# Revit family: Gohome_ClubOttoman_R19
name_source: partatom
category: Furniture
units: mm (PartAtom-declared; Revit-internal decimal feet)

## family parameters
Always vertical = Yes
Cut with Voids When Loaded = No
OmniClass Number = 23.40.20.00
OmniClass Title = General Furniture and Specialties
Room Calculation Point = No
Shared = No
Work Plane-Based = No

## types (4) — shared parameters
Depth = 700 mm  [stored 2.29659 ft]
Manufacturer = gohome
Seat Height = 450 mm  [stored 1.47638 ft]
Timber Leg Material = <By Category>
URL = www.gohome.com.au
Upholstery Material = <By Category>
Width = 1800 mm  [stored 5.90551 ft]

## per-type parameters (varying)
| type | Height | ShowCenterBottomLeg | ShowCenterTopLeg | ShowEndLeg | With Bolster | With Tabletop Center | With Tabletop End |
| Club Ottoman w/4 Legs | 450 mm  [stored 1.47638 ft] | Yes | Yes | Yes | No | No | No |
| Club Ottoman w/Bolster | 605 mm  [stored 1.98491 ft] | No | No | Yes | Yes | No | No |
| Club Ottoman w/Tabletop Center | 600 mm | No | Yes | Yes | No | Yes | No |
| Club Ottoman w/Tabletop End | 600 mm | Yes | Yes | No | No | No | Yes |

note: column(s) folded — value = type name in every type: Model

note: [stored X ft] marks values corroborated as IEEE doubles in the binary element streams (Revit-internal decimal feet)

## geometry (parser evidence)
native form markers: Sweep x2
no freeform markers — native parametric forms only
